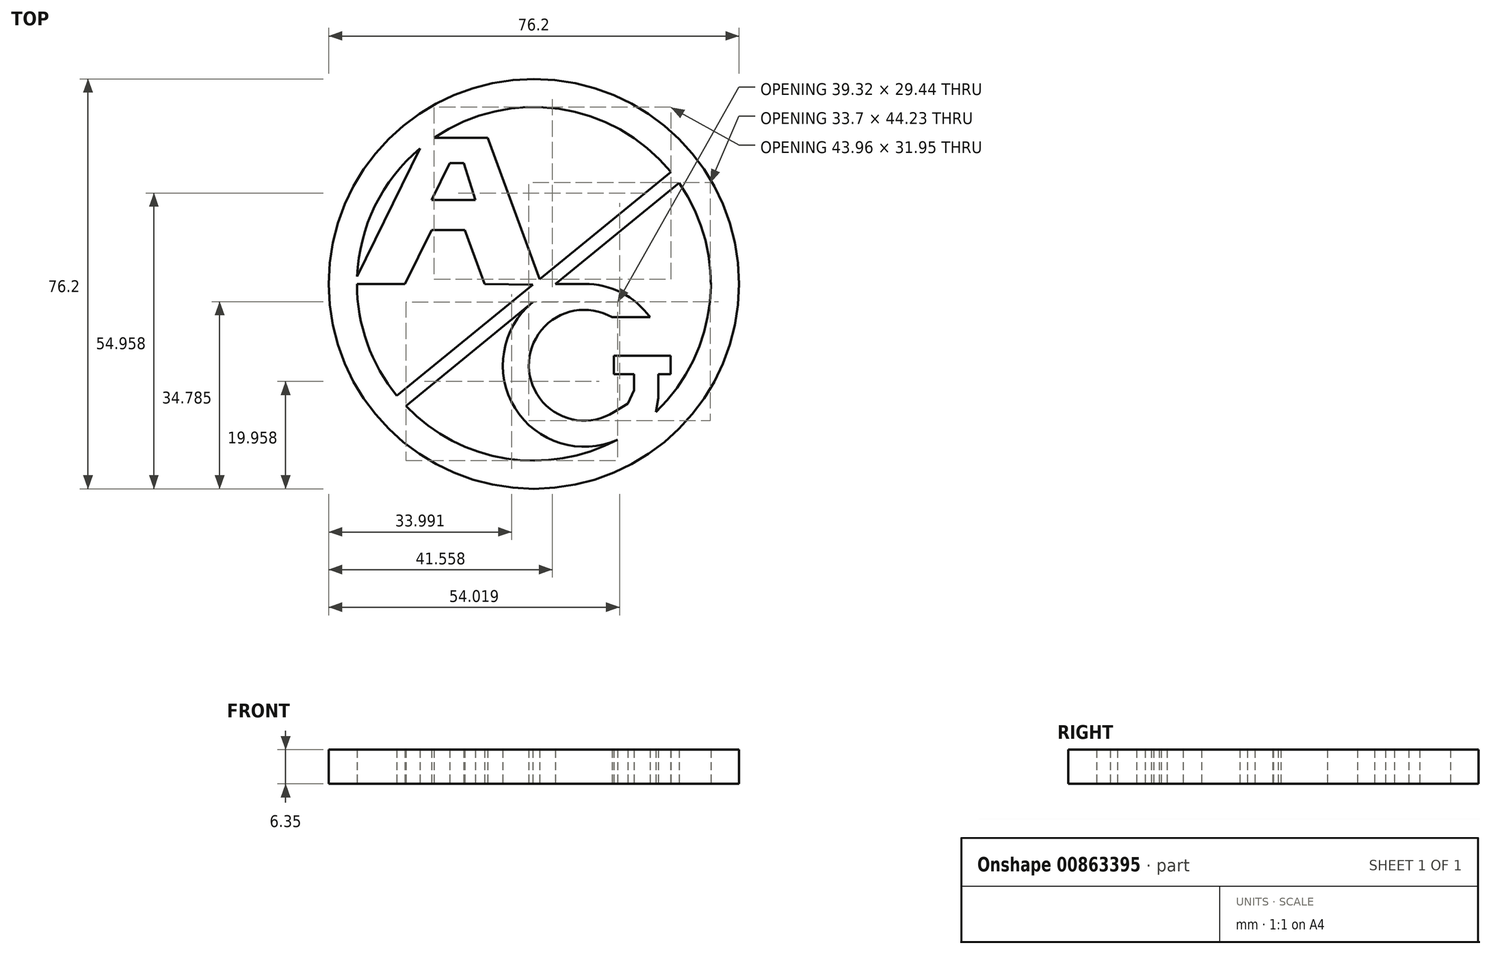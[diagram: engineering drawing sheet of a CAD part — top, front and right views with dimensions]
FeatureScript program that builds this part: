
annotation { "Feature Type Name" : "Feature", "Feature Type Description" : "" }
export const myFeature = defineFeature(function(context is Context, id is Id, definition is map)
    precondition{}
    {
        {
            var Q0;
            Q0=qCreatedBy(makeId("Top.planeOp"),FACE);
            var sketch = newSketch(context, id + "F0", { "sketchPlane" : qUnion([Q0])});
            skCircle(sketch, "E0", {"center": v(0, 0) * mm, "radius": 38.1 * mm});
            skArc(sketch, "E1", {"start": v(-23.77, -22.7) * mm, "mid": v(-5.16, -32.45) * mm, "end": v(15.55, -28.95) * mm});
            skLineSegment(sketch, "E2", {"start": v(-32.86, 0) * mm, "end": v(-23.93, 0) * mm});
            skLineSegment(sketch, "E3", {"start": v(-9.14, 0) * mm, "end": v(-0.2, -0.17) * mm});
            skLineSegment(sketch, "E4", {"start": v(-23.93, 0) * mm, "end": v(-19, 10.03) * mm});
            skLineSegment(sketch, "E5", {"start": v(-32.85, 1.32) * mm, "end": v(-21.14, 25.16) * mm});
            skLineSegment(sketch, "E6", {"start": v(-9.14, 0) * mm, "end": v(-12.81, 10.03) * mm});
            skLineSegment(sketch, "E7", {"start": v(-19, 10.03) * mm, "end": v(-12.81, 10.03) * mm});
            skLineSegment(sketch, "E8", {"start": v(-19, 15.6) * mm, "end": v(-10.83, 15.6) * mm});
            skLineSegment(sketch, "E9", {"start": v(-10.83, 15.6) * mm, "end": v(-13, 22.48) * mm});
            skLineSegment(sketch, "E10", {"start": v(-13, 22.48) * mm, "end": v(-15.62, 22.48) * mm});
            skLineSegment(sketch, "E11", {"start": v(-15.62, 22.48) * mm, "end": v(-19, 15.6) * mm});
            skLineSegment(sketch, "E12", {"start": v(32.86, 0) * mm, "end": v(3.97, 0) * mm, "construction": true});
            skLineSegment(sketch, "E13", {"start": v(-13.7, -27.5) * mm, "end": v(-2.73, -5.48) * mm, "construction": true});
            skArc(sketch, "E14", {"start": v(21.6, -6.21) * mm, "mid": v(16.23, -1.64) * mm, "end": v(9.37, 0) * mm});
            skLineSegment(sketch, "E15.bottom", {"start": v(14.88, -16.77) * mm, "end": v(18.59, -16.77) * mm});
            skLineSegment(sketch, "E15.top", {"start": v(14.88, -13.34) * mm, "end": v(25.43, -13.34) * mm});
            skLineSegment(sketch, "E15.left", {"start": v(14.88, -16.77) * mm, "end": v(14.88, -13.34) * mm});
            skLineSegment(sketch, "E15.right", {"start": v(25.43, -16.77) * mm, "end": v(25.43, -13.34) * mm});
            skArc(sketch, "E16", {"start": v(14.52, -6.21) * mm, "mid": v(-0.93, -15.34) * mm, "end": v(14.88, -23.84) * mm});
            skLineSegment(sketch, "E17", {"start": v(21.6, -6.21) * mm, "end": v(14.52, -6.21) * mm});
            skLineSegment(sketch, "E18", {"start": v(-23.77, -22.7) * mm, "end": v(-0.21, -3.42) * mm});
            skLineSegment(sketch, "E19", {"start": v(0, 0) * mm, "end": v(-25.44, -20.8) * mm});
            skLineSegment(sketch, "E20", {"start": v(1.08, 0.88) * mm, "end": v(25.44, 20.8) * mm});
            skArc(sketch, "E21.trimOffspring", {"start": v(25.44, 20.8) * mm, "mid": v(4.7, 32.53) * mm, "end": v(-18.52, 27.15) * mm});
            skArc(sketch, "E22.trimOffspring", {"start": v(22.65, -23.81) * mm, "mid": v(32.7, -3.3) * mm, "end": v(26.95, 18.8) * mm});
            skArc(sketch, "E23.trimOffspring", {"start": v(-0.21, -3.42) * mm, "mid": v(-3.5, -23.09) * mm, "end": v(15.55, -28.95) * mm});
            skLineSegment(sketch, "E24.trimOffspring", {"start": v(3.97, 0) * mm, "end": v(26.95, 18.8) * mm});
            skLineSegment(sketch, "E25", {"start": v(-8.55, 27.15) * mm, "end": v(-18.52, 27.15) * mm});
            skArc(sketch, "E26.trimOffspring", {"start": v(-21.14, 25.16) * mm, "mid": v(-29.5, 14.49) * mm, "end": v(-32.84, 1.35) * mm});
            skLineSegment(sketch, "E27", {"start": v(9.37, 0) * mm, "end": v(3.97, 0) * mm});
            skLineSegment(sketch, "E28", {"start": v(14.88, -23.84) * mm, "end": v(17.44, -22.22) * mm});
            skLineSegment(sketch, "E29", {"start": v(17.44, -22.22) * mm, "end": v(18.59, -19.76) * mm});
            skLineSegment(sketch, "E30", {"start": v(18.59, -19.76) * mm, "end": v(18.59, -16.77) * mm});
            skLineSegment(sketch, "E31", {"start": v(22.65, -23.81) * mm, "end": v(23.13, -21.22) * mm});
            skLineSegment(sketch, "E32", {"start": v(23.13, -21.22) * mm, "end": v(23.13, -18.5) * mm});
            skLineSegment(sketch, "E33", {"start": v(23.13, -18.5) * mm, "end": v(23.13, -16.77) * mm});
            skLineSegment(sketch, "E34.trimOffspring", {"start": v(23.13, -16.77) * mm, "end": v(25.43, -16.77) * mm});
            skArc(sketch, "E35.trimOffspring", {"start": v(-32.86, 0) * mm, "mid": v(-30.95, -11.05) * mm, "end": v(-25.44, -20.8) * mm});
            skLineSegment(sketch, "E36", {"start": v(-8.55, 27.15) * mm, "end": v(1.08, 0.88) * mm});
            skSolve(sketch);
        }
        {
            var Q0;
            Q0=makeQuery(id+"F0.imprint","IMPRINT",FACE,{"disambiguationData":[TD([[makeQuery(id+"F0.imprint","IMPRINT",EDGE,{"derivedFrom":sQuery(id+"F0.wireOp",EDGE,"E0")}),1.0]])]});
            extrude(context, id + "F1", {"entities" : qUnion([Q0]), "depth" : 6.35 * mm, "offsetDistance" : 25.4 * mm});
        }
    });
